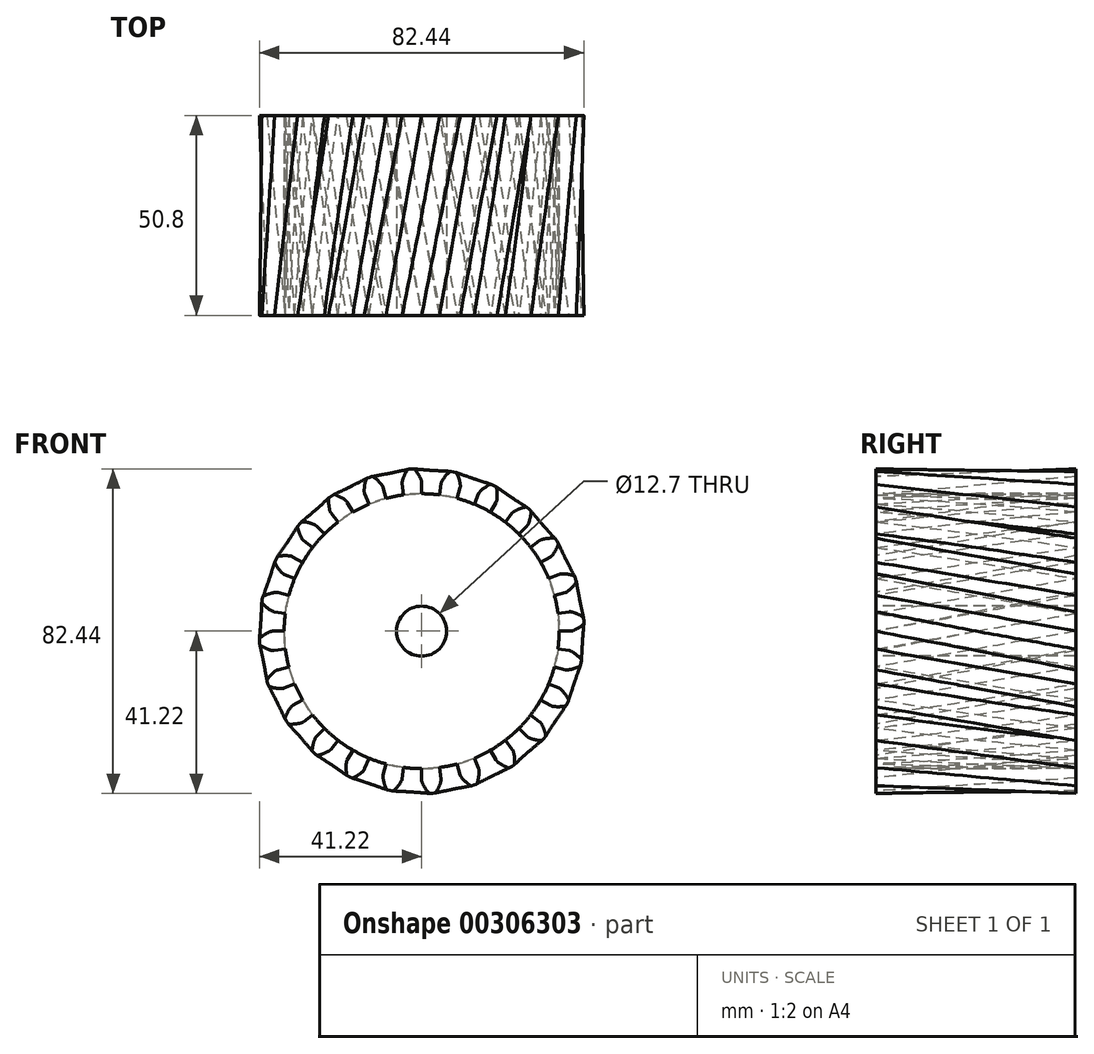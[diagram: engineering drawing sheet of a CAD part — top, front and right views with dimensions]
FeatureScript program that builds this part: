
annotation { "Feature Type Name" : "Feature", "Feature Type Description" : "" }
export const myFeature = defineFeature(function(context is Context, id is Id, definition is map)
    precondition{}
    {
        {
            var Q0;
            Q0=qCreatedBy(makeId("Front.planeOp"),FACE);
            var sketch = newSketch(context, id + "F0", { "sketchPlane" : qUnion([Q0])});
            skCircle(sketch, "E0", {"center": v(0, 0) * mm, "radius": 34.93 * mm});
            skArc(sketch, "E1.trimOffspring", {"start": v(-0.11, 38.4) * mm, "mid": v(-0.8, 39.79) * mm, "end": v(-1.72, 41.04) * mm});
            skLineSegment(sketch, "E2", {"start": v(0, 37.8) * mm, "end": v(0, 34.93) * mm});
            skLineSegment(sketch, "E3", {"start": v(-2.13, 41.22) * mm, "end": v(-2.7, 41.2) * mm});
            skArc(sketch, "E4.MirrorCS", {"start": v(-4.9, 38.09) * mm, "mid": v(-4.4, 39.55) * mm, "end": v(-3.65, 40.92) * mm});
            skLineSegment(sketch, "E5.MirrorCS", {"start": v(-4.93, 37.48) * mm, "end": v(-4.56, 34.63) * mm});
            skLineSegment(sketch, "E6.MirrorCS", {"start": v(-3.27, 41.15) * mm, "end": v(-2.7, 41.2) * mm});
            skPoint(sketch, "E7.visualSharp", {"position": v(-3.51, 41.13) * mm});
            skArc(sketch, "E7.filletArc", {"start": v(-3.27, 41.15) * mm, "mid": v(-3.49, 41.08) * mm, "end": v(-3.65, 40.92) * mm});
            skPoint(sketch, "E8.visualSharp", {"position": v(-1.89, 41.23) * mm});
            skArc(sketch, "E8.filletArc", {"start": v(-1.72, 41.04) * mm, "mid": v(-1.9, 41.18) * mm, "end": v(-2.13, 41.22) * mm});
            skPoint(sketch, "E9.visualSharp", {"position": v(-4.97, 37.77) * mm});
            skArc(sketch, "E9.filletArc", {"start": v(-4.9, 38.09) * mm, "mid": v(-4.95, 37.79) * mm, "end": v(-4.93, 37.48) * mm});
            skPoint(sketch, "E10.visualSharp", {"position": v(0, 38.1) * mm});
            skArc(sketch, "E10.filletArc", {"start": v(0, 37.8) * mm, "mid": v(-0.03, 38.1) * mm, "end": v(-0.11, 38.4) * mm});
            skSolve(sketch);
        }
        {
            var Q0;
            {var subQ0=sQuery(id+"F0.wireOp",EDGE,"E0");var subQ1=makeQuery(id+"F0.imprint","INTERSECT",VERTEX,{"derivedFrom":[subQ0,sQuery(id+"F0.wireOp",EDGE,"E2")]});Q0=makeQuery(id+"F0.imprint","IMPRINT",FACE,{"disambiguationData":[TD([[makeQuery(id+"F0.imprint","IMPRINT",EDGE,{"disambiguationData":[TD([[subQ1,-1.0]])],"derivedFrom":subQ0}),1.0]])]});}
            cPlane(context, id + "F1", {"entities" : qUnion([Q0]), "cplaneType" : CPlaneType.OFFSET, "offset" : 50.8 * mm, "width" : 152.4 * mm, "height" : 152.4 * mm});
        }
        {
            var Q0;
            Q0=qCreatedBy(id+"F1.planeOp",FACE);
            var sketch = newSketch(context, id + "F2", { "sketchPlane" : qUnion([Q0])});
            skCircle(sketch, "E11.0", {"center": v(0, 0) * mm, "radius": 34.93 * mm});
            skArc(sketch, "E12.0.0", {"start": v(-3.65, 40.92) * mm, "mid": v(-4.4, 39.55) * mm, "end": v(-4.9, 38.09) * mm});
            skArc(sketch, "E12.0.1", {"start": v(-4.9, 38.09) * mm, "mid": v(-4.95, 37.79) * mm, "end": v(-4.93, 37.48) * mm});
            skLineSegment(sketch, "E12.0.2", {"start": v(-4.93, 37.48) * mm, "end": v(-4.56, 34.63) * mm});
            skArc(sketch, "E12.0.3", {"start": v(-4.56, 34.63) * mm, "mid": v(-2.28, 34.85) * mm, "end": v(0, 34.93) * mm});
            skLineSegment(sketch, "E12.0.4", {"start": v(0, 34.93) * mm, "end": v(0, 37.8) * mm});
            skArc(sketch, "E12.0.5", {"start": v(0, 37.8) * mm, "mid": v(-0.03, 38.1) * mm, "end": v(-0.11, 38.4) * mm});
            skArc(sketch, "E12.0.6", {"start": v(-0.11, 38.4) * mm, "mid": v(-0.8, 39.79) * mm, "end": v(-1.72, 41.04) * mm});
            skArc(sketch, "E12.0.7", {"start": v(-1.72, 41.04) * mm, "mid": v(-1.9, 41.18) * mm, "end": v(-2.13, 41.22) * mm});
            skLineSegment(sketch, "E12.0.8", {"start": v(-2.13, 41.22) * mm, "end": v(-2.7, 41.2) * mm});
            skLineSegment(sketch, "E12.0.9", {"start": v(-2.7, 41.2) * mm, "end": v(-3.27, 41.15) * mm});
            skArc(sketch, "E12.0.10", {"start": v(-3.27, 41.15) * mm, "mid": v(-3.49, 41.08) * mm, "end": v(-3.65, 40.92) * mm});
            skLineSegment(sketch, "E13.1.0", {"start": v(-9.04, 33.73) * mm, "end": v(-9.79, 36.52) * mm});
            skArc(sketch, "E13.1.1", {"start": v(-10.05, 37.06) * mm, "mid": v(-11.08, 38.22) * mm, "end": v(-12.29, 39.2) * mm});
            skArc(sketch, "E13.1.2", {"start": v(-14.12, 38.58) * mm, "mid": v(-14.48, 37.07) * mm, "end": v(-14.59, 35.52) * mm});
            skLineSegment(sketch, "E13.1.3", {"start": v(-14.47, 34.93) * mm, "end": v(-13.37, 32.27) * mm});
            skArc(sketch, "E13.1.4", {"start": v(-14.59, 35.52) * mm, "mid": v(-14.56, 35.22) * mm, "end": v(-14.47, 34.93) * mm});
            skArc(sketch, "E13.1.5", {"start": v(-9.79, 36.52) * mm, "mid": v(-9.9, 36.8) * mm, "end": v(-10.05, 37.06) * mm});
            skArc(sketch, "E13.1.6", {"start": v(-12.29, 39.2) * mm, "mid": v(-12.5, 39.28) * mm, "end": v(-12.73, 39.26) * mm});
            skLineSegment(sketch, "E13.1.7", {"start": v(-12.73, 39.26) * mm, "end": v(-13.27, 39.1) * mm});
            skLineSegment(sketch, "E13.1.8", {"start": v(-13.27, 39.1) * mm, "end": v(-13.8, 38.9) * mm});
            skArc(sketch, "E13.1.9", {"start": v(-13.8, 38.9) * mm, "mid": v(-14, 38.77) * mm, "end": v(-14.12, 38.58) * mm});
            skLineSegment(sketch, "E13.2.0", {"start": v(-17.46, 30.25) * mm, "end": v(-18.9, 32.74) * mm});
            skArc(sketch, "E13.2.1", {"start": v(-19.3, 33.2) * mm, "mid": v(-20.6, 34.05) * mm, "end": v(-22.01, 34.68) * mm});
            skArc(sketch, "E13.2.2", {"start": v(-23.62, 33.61) * mm, "mid": v(-23.58, 32.06) * mm, "end": v(-23.29, 30.53) * mm});
            skLineSegment(sketch, "E13.2.3", {"start": v(-23.02, 30) * mm, "end": v(-21.26, 27.7) * mm});
            skArc(sketch, "E13.2.4", {"start": v(-23.29, 30.53) * mm, "mid": v(-23.18, 30.25) * mm, "end": v(-23.02, 30) * mm});
            skArc(sketch, "E13.2.5", {"start": v(-18.9, 32.74) * mm, "mid": v(-19.08, 32.99) * mm, "end": v(-19.3, 33.2) * mm});
            skArc(sketch, "E13.2.6", {"start": v(-22.01, 34.68) * mm, "mid": v(-22.24, 34.7) * mm, "end": v(-22.45, 34.63) * mm});
            skLineSegment(sketch, "E13.2.7", {"start": v(-22.45, 34.63) * mm, "end": v(-22.94, 34.33) * mm});
            skLineSegment(sketch, "E13.2.8", {"start": v(-22.94, 34.33) * mm, "end": v(-23.4, 34) * mm});
            skArc(sketch, "E13.2.9", {"start": v(-23.4, 34) * mm, "mid": v(-23.56, 33.83) * mm, "end": v(-23.62, 33.61) * mm});
            skLineSegment(sketch, "E13.3.0", {"start": v(-24.7, 24.7) * mm, "end": v(-26.73, 26.73) * mm});
            skArc(sketch, "E13.3.1", {"start": v(-27.23, 27.07) * mm, "mid": v(-28.7, 27.56) * mm, "end": v(-30.24, 27.8) * mm});
            skArc(sketch, "E13.3.2", {"start": v(-31.51, 26.35) * mm, "mid": v(-31.07, 24.86) * mm, "end": v(-30.4, 23.47) * mm});
            skLineSegment(sketch, "E13.3.3", {"start": v(-30, 23.02) * mm, "end": v(-27.7, 21.26) * mm});
            skArc(sketch, "E13.3.4", {"start": v(-30.4, 23.47) * mm, "mid": v(-30.22, 23.22) * mm, "end": v(-30, 23.02) * mm});
            skArc(sketch, "E13.3.5", {"start": v(-26.73, 26.73) * mm, "mid": v(-26.97, 26.93) * mm, "end": v(-27.23, 27.07) * mm});
            skArc(sketch, "E13.3.6", {"start": v(-30.24, 27.8) * mm, "mid": v(-30.47, 27.77) * mm, "end": v(-30.65, 27.64) * mm});
            skLineSegment(sketch, "E13.3.7", {"start": v(-30.65, 27.64) * mm, "end": v(-31.04, 27.22) * mm});
            skLineSegment(sketch, "E13.3.8", {"start": v(-31.04, 27.22) * mm, "end": v(-31.4, 26.78) * mm});
            skArc(sketch, "E13.3.9", {"start": v(-31.4, 26.78) * mm, "mid": v(-31.51, 26.58) * mm, "end": v(-31.51, 26.35) * mm});
            skLineSegment(sketch, "E13.4.0", {"start": v(-30.25, 17.46) * mm, "end": v(-32.74, 18.9) * mm});
            skArc(sketch, "E13.4.1", {"start": v(-33.31, 19.1) * mm, "mid": v(-34.86, 19.2) * mm, "end": v(-36.4, 19.03) * mm});
            skArc(sketch, "E13.4.2", {"start": v(-37.26, 17.3) * mm, "mid": v(-36.45, 15.97) * mm, "end": v(-35.43, 14.8) * mm});
            skLineSegment(sketch, "E13.4.3", {"start": v(-34.93, 14.47) * mm, "end": v(-32.27, 13.37) * mm});
            skArc(sketch, "E13.4.4", {"start": v(-35.43, 14.8) * mm, "mid": v(-35.2, 14.61) * mm, "end": v(-34.93, 14.47) * mm});
            skArc(sketch, "E13.4.5", {"start": v(-32.74, 18.9) * mm, "mid": v(-33.02, 19.03) * mm, "end": v(-33.31, 19.1) * mm});
            skArc(sketch, "E13.4.6", {"start": v(-36.4, 19.03) * mm, "mid": v(-36.62, 18.94) * mm, "end": v(-36.76, 18.77) * mm});
            skLineSegment(sketch, "E13.4.7", {"start": v(-36.76, 18.77) * mm, "end": v(-37.03, 18.26) * mm});
            skLineSegment(sketch, "E13.4.8", {"start": v(-37.03, 18.26) * mm, "end": v(-37.27, 17.74) * mm});
            skArc(sketch, "E13.4.9", {"start": v(-37.27, 17.74) * mm, "mid": v(-37.32, 17.52) * mm, "end": v(-37.26, 17.3) * mm});
            skLineSegment(sketch, "E13.5.0", {"start": v(-33.73, 9.04) * mm, "end": v(-36.52, 9.79) * mm});
            skArc(sketch, "E13.5.1", {"start": v(-37.12, 9.83) * mm, "mid": v(-38.64, 9.52) * mm, "end": v(-40.1, 8.96) * mm});
            skArc(sketch, "E13.5.2", {"start": v(-40.47, 7.06) * mm, "mid": v(-39.34, 6) * mm, "end": v(-38.06, 5.13) * mm});
            skLineSegment(sketch, "E13.5.3", {"start": v(-37.48, 4.93) * mm, "end": v(-34.63, 4.56) * mm});
            skArc(sketch, "E13.5.4", {"start": v(-38.06, 5.13) * mm, "mid": v(-37.78, 5) * mm, "end": v(-37.48, 4.93) * mm});
            skArc(sketch, "E13.5.5", {"start": v(-36.52, 9.79) * mm, "mid": v(-36.82, 9.84) * mm, "end": v(-37.12, 9.83) * mm});
            skArc(sketch, "E13.5.6", {"start": v(-40.1, 8.96) * mm, "mid": v(-40.27, 8.82) * mm, "end": v(-40.37, 8.61) * mm});
            skLineSegment(sketch, "E13.5.7", {"start": v(-40.37, 8.61) * mm, "end": v(-40.49, 8.05) * mm});
            skLineSegment(sketch, "E13.5.8", {"start": v(-40.49, 8.05) * mm, "end": v(-40.6, 7.5) * mm});
            skArc(sketch, "E13.5.9", {"start": v(-40.6, 7.5) * mm, "mid": v(-40.58, 7.26) * mm, "end": v(-40.47, 7.06) * mm});
            skLineSegment(sketch, "E13.6.0", {"start": v(-34.93, 0) * mm, "end": v(-37.8, 0) * mm});
            skArc(sketch, "E13.6.1", {"start": v(-38.4, -0.11) * mm, "mid": v(-39.79, -0.8) * mm, "end": v(-41.04, -1.72) * mm});
            skArc(sketch, "E13.6.2", {"start": v(-40.92, -3.65) * mm, "mid": v(-39.55, -4.4) * mm, "end": v(-38.09, -4.9) * mm});
            skLineSegment(sketch, "E13.6.3", {"start": v(-37.48, -4.93) * mm, "end": v(-34.63, -4.56) * mm});
            skArc(sketch, "E13.6.4", {"start": v(-38.09, -4.9) * mm, "mid": v(-37.79, -4.95) * mm, "end": v(-37.48, -4.93) * mm});
            skArc(sketch, "E13.6.5", {"start": v(-37.8, 0) * mm, "mid": v(-38.1, -0.03) * mm, "end": v(-38.4, -0.11) * mm});
            skArc(sketch, "E13.6.6", {"start": v(-41.04, -1.72) * mm, "mid": v(-41.18, -1.9) * mm, "end": v(-41.22, -2.13) * mm});
            skLineSegment(sketch, "E13.6.7", {"start": v(-41.22, -2.13) * mm, "end": v(-41.2, -2.7) * mm});
            skLineSegment(sketch, "E13.6.8", {"start": v(-41.2, -2.7) * mm, "end": v(-41.15, -3.27) * mm});
            skArc(sketch, "E13.6.9", {"start": v(-41.15, -3.27) * mm, "mid": v(-41.08, -3.49) * mm, "end": v(-40.92, -3.65) * mm});
            skLineSegment(sketch, "E13.7.0", {"start": v(-33.73, -9.04) * mm, "end": v(-36.52, -9.79) * mm});
            skArc(sketch, "E13.7.1", {"start": v(-37.06, -10.05) * mm, "mid": v(-38.22, -11.08) * mm, "end": v(-39.2, -12.29) * mm});
            skArc(sketch, "E13.7.2", {"start": v(-38.58, -14.12) * mm, "mid": v(-37.07, -14.48) * mm, "end": v(-35.52, -14.59) * mm});
            skLineSegment(sketch, "E13.7.3", {"start": v(-34.93, -14.47) * mm, "end": v(-32.27, -13.37) * mm});
            skArc(sketch, "E13.7.4", {"start": v(-35.52, -14.59) * mm, "mid": v(-35.22, -14.56) * mm, "end": v(-34.93, -14.47) * mm});
            skArc(sketch, "E13.7.5", {"start": v(-36.52, -9.79) * mm, "mid": v(-36.8, -9.9) * mm, "end": v(-37.06, -10.05) * mm});
            skArc(sketch, "E13.7.6", {"start": v(-39.2, -12.29) * mm, "mid": v(-39.28, -12.5) * mm, "end": v(-39.26, -12.73) * mm});
            skLineSegment(sketch, "E13.7.7", {"start": v(-39.26, -12.73) * mm, "end": v(-39.1, -13.27) * mm});
            skLineSegment(sketch, "E13.7.8", {"start": v(-39.1, -13.27) * mm, "end": v(-38.9, -13.8) * mm});
            skArc(sketch, "E13.7.9", {"start": v(-38.9, -13.8) * mm, "mid": v(-38.77, -14) * mm, "end": v(-38.58, -14.12) * mm});
            skLineSegment(sketch, "E13.8.0", {"start": v(-30.25, -17.46) * mm, "end": v(-32.74, -18.9) * mm});
            skArc(sketch, "E13.8.1", {"start": v(-33.2, -19.3) * mm, "mid": v(-34.05, -20.6) * mm, "end": v(-34.68, -22.01) * mm});
            skArc(sketch, "E13.8.2", {"start": v(-33.61, -23.62) * mm, "mid": v(-32.06, -23.58) * mm, "end": v(-30.53, -23.29) * mm});
            skLineSegment(sketch, "E13.8.3", {"start": v(-30, -23.02) * mm, "end": v(-27.7, -21.26) * mm});
            skArc(sketch, "E13.8.4", {"start": v(-30.53, -23.29) * mm, "mid": v(-30.25, -23.18) * mm, "end": v(-30, -23.02) * mm});
            skArc(sketch, "E13.8.5", {"start": v(-32.74, -18.9) * mm, "mid": v(-32.99, -19.08) * mm, "end": v(-33.2, -19.3) * mm});
            skArc(sketch, "E13.8.6", {"start": v(-34.68, -22.01) * mm, "mid": v(-34.7, -22.24) * mm, "end": v(-34.63, -22.45) * mm});
            skLineSegment(sketch, "E13.8.7", {"start": v(-34.63, -22.45) * mm, "end": v(-34.33, -22.94) * mm});
            skLineSegment(sketch, "E13.8.8", {"start": v(-34.33, -22.94) * mm, "end": v(-34, -23.4) * mm});
            skArc(sketch, "E13.8.9", {"start": v(-34, -23.4) * mm, "mid": v(-33.83, -23.56) * mm, "end": v(-33.61, -23.62) * mm});
            skLineSegment(sketch, "E13.9.0", {"start": v(-24.7, -24.7) * mm, "end": v(-26.73, -26.73) * mm});
            skArc(sketch, "E13.9.1", {"start": v(-27.07, -27.23) * mm, "mid": v(-27.56, -28.7) * mm, "end": v(-27.8, -30.24) * mm});
            skArc(sketch, "E13.9.2", {"start": v(-26.35, -31.51) * mm, "mid": v(-24.86, -31.07) * mm, "end": v(-23.47, -30.4) * mm});
            skLineSegment(sketch, "E13.9.3", {"start": v(-23.02, -30) * mm, "end": v(-21.26, -27.7) * mm});
            skArc(sketch, "E13.9.4", {"start": v(-23.47, -30.4) * mm, "mid": v(-23.22, -30.22) * mm, "end": v(-23.02, -30) * mm});
            skArc(sketch, "E13.9.5", {"start": v(-26.73, -26.73) * mm, "mid": v(-26.93, -26.97) * mm, "end": v(-27.07, -27.23) * mm});
            skArc(sketch, "E13.9.6", {"start": v(-27.8, -30.24) * mm, "mid": v(-27.77, -30.47) * mm, "end": v(-27.64, -30.65) * mm});
            skLineSegment(sketch, "E13.9.7", {"start": v(-27.64, -30.65) * mm, "end": v(-27.22, -31.04) * mm});
            skLineSegment(sketch, "E13.9.8", {"start": v(-27.22, -31.04) * mm, "end": v(-26.78, -31.4) * mm});
            skArc(sketch, "E13.9.9", {"start": v(-26.78, -31.4) * mm, "mid": v(-26.58, -31.51) * mm, "end": v(-26.35, -31.51) * mm});
            skLineSegment(sketch, "E13.10.0", {"start": v(-17.46, -30.25) * mm, "end": v(-18.9, -32.74) * mm});
            skArc(sketch, "E13.10.1", {"start": v(-19.1, -33.31) * mm, "mid": v(-19.2, -34.86) * mm, "end": v(-19.03, -36.4) * mm});
            skArc(sketch, "E13.10.2", {"start": v(-17.3, -37.26) * mm, "mid": v(-15.97, -36.45) * mm, "end": v(-14.8, -35.43) * mm});
            skLineSegment(sketch, "E13.10.3", {"start": v(-14.47, -34.93) * mm, "end": v(-13.37, -32.27) * mm});
            skArc(sketch, "E13.10.4", {"start": v(-14.8, -35.43) * mm, "mid": v(-14.61, -35.2) * mm, "end": v(-14.47, -34.93) * mm});
            skArc(sketch, "E13.10.5", {"start": v(-18.9, -32.74) * mm, "mid": v(-19.03, -33.02) * mm, "end": v(-19.1, -33.31) * mm});
            skArc(sketch, "E13.10.6", {"start": v(-19.03, -36.4) * mm, "mid": v(-18.94, -36.62) * mm, "end": v(-18.77, -36.76) * mm});
            skLineSegment(sketch, "E13.10.7", {"start": v(-18.77, -36.76) * mm, "end": v(-18.26, -37.03) * mm});
            skLineSegment(sketch, "E13.10.8", {"start": v(-18.26, -37.03) * mm, "end": v(-17.74, -37.27) * mm});
            skArc(sketch, "E13.10.9", {"start": v(-17.74, -37.27) * mm, "mid": v(-17.52, -37.32) * mm, "end": v(-17.3, -37.26) * mm});
            skLineSegment(sketch, "E13.11.0", {"start": v(-9.04, -33.73) * mm, "end": v(-9.79, -36.52) * mm});
            skArc(sketch, "E13.11.1", {"start": v(-9.83, -37.12) * mm, "mid": v(-9.52, -38.64) * mm, "end": v(-8.96, -40.1) * mm});
            skArc(sketch, "E13.11.2", {"start": v(-7.06, -40.47) * mm, "mid": v(-6, -39.34) * mm, "end": v(-5.13, -38.06) * mm});
            skLineSegment(sketch, "E13.11.3", {"start": v(-4.93, -37.48) * mm, "end": v(-4.56, -34.63) * mm});
            skArc(sketch, "E13.11.4", {"start": v(-5.13, -38.06) * mm, "mid": v(-5, -37.78) * mm, "end": v(-4.93, -37.48) * mm});
            skArc(sketch, "E13.11.5", {"start": v(-9.79, -36.52) * mm, "mid": v(-9.84, -36.82) * mm, "end": v(-9.83, -37.12) * mm});
            skArc(sketch, "E13.11.6", {"start": v(-8.96, -40.1) * mm, "mid": v(-8.82, -40.27) * mm, "end": v(-8.61, -40.37) * mm});
            skLineSegment(sketch, "E13.11.7", {"start": v(-8.61, -40.37) * mm, "end": v(-8.05, -40.49) * mm});
            skLineSegment(sketch, "E13.11.8", {"start": v(-8.05, -40.49) * mm, "end": v(-7.5, -40.6) * mm});
            skArc(sketch, "E13.11.9", {"start": v(-7.5, -40.6) * mm, "mid": v(-7.26, -40.58) * mm, "end": v(-7.06, -40.47) * mm});
            skLineSegment(sketch, "E13.12.0", {"start": v(0, -34.93) * mm, "end": v(0, -37.8) * mm});
            skArc(sketch, "E13.12.1", {"start": v(0.11, -38.4) * mm, "mid": v(0.8, -39.79) * mm, "end": v(1.72, -41.04) * mm});
            skArc(sketch, "E13.12.2", {"start": v(3.65, -40.92) * mm, "mid": v(4.4, -39.55) * mm, "end": v(4.9, -38.09) * mm});
            skLineSegment(sketch, "E13.12.3", {"start": v(4.93, -37.48) * mm, "end": v(4.56, -34.63) * mm});
            skArc(sketch, "E13.12.4", {"start": v(4.9, -38.09) * mm, "mid": v(4.95, -37.79) * mm, "end": v(4.93, -37.48) * mm});
            skArc(sketch, "E13.12.5", {"start": v(0, -37.8) * mm, "mid": v(0.03, -38.1) * mm, "end": v(0.11, -38.4) * mm});
            skArc(sketch, "E13.12.6", {"start": v(1.72, -41.04) * mm, "mid": v(1.9, -41.18) * mm, "end": v(2.13, -41.22) * mm});
            skLineSegment(sketch, "E13.12.7", {"start": v(2.13, -41.22) * mm, "end": v(2.7, -41.2) * mm});
            skLineSegment(sketch, "E13.12.8", {"start": v(2.7, -41.2) * mm, "end": v(3.27, -41.15) * mm});
            skArc(sketch, "E13.12.9", {"start": v(3.27, -41.15) * mm, "mid": v(3.49, -41.08) * mm, "end": v(3.65, -40.92) * mm});
            skLineSegment(sketch, "E13.13.0", {"start": v(9.04, -33.73) * mm, "end": v(9.79, -36.52) * mm});
            skArc(sketch, "E13.13.1", {"start": v(10.05, -37.06) * mm, "mid": v(11.08, -38.22) * mm, "end": v(12.29, -39.2) * mm});
            skArc(sketch, "E13.13.2", {"start": v(14.12, -38.58) * mm, "mid": v(14.48, -37.07) * mm, "end": v(14.59, -35.52) * mm});
            skLineSegment(sketch, "E13.13.3", {"start": v(14.47, -34.93) * mm, "end": v(13.37, -32.27) * mm});
            skArc(sketch, "E13.13.4", {"start": v(14.59, -35.52) * mm, "mid": v(14.56, -35.22) * mm, "end": v(14.47, -34.93) * mm});
            skArc(sketch, "E13.13.5", {"start": v(9.79, -36.52) * mm, "mid": v(9.9, -36.8) * mm, "end": v(10.05, -37.06) * mm});
            skArc(sketch, "E13.13.6", {"start": v(12.29, -39.2) * mm, "mid": v(12.5, -39.28) * mm, "end": v(12.73, -39.26) * mm});
            skLineSegment(sketch, "E13.13.7", {"start": v(12.73, -39.26) * mm, "end": v(13.27, -39.1) * mm});
            skLineSegment(sketch, "E13.13.8", {"start": v(13.27, -39.1) * mm, "end": v(13.8, -38.9) * mm});
            skArc(sketch, "E13.13.9", {"start": v(13.8, -38.9) * mm, "mid": v(14, -38.77) * mm, "end": v(14.12, -38.58) * mm});
            skLineSegment(sketch, "E13.14.0", {"start": v(17.46, -30.25) * mm, "end": v(18.9, -32.74) * mm});
            skArc(sketch, "E13.14.1", {"start": v(19.3, -33.2) * mm, "mid": v(20.6, -34.05) * mm, "end": v(22.01, -34.68) * mm});
            skArc(sketch, "E13.14.2", {"start": v(23.62, -33.61) * mm, "mid": v(23.58, -32.06) * mm, "end": v(23.29, -30.53) * mm});
            skLineSegment(sketch, "E13.14.3", {"start": v(23.02, -30) * mm, "end": v(21.26, -27.7) * mm});
            skArc(sketch, "E13.14.4", {"start": v(23.29, -30.53) * mm, "mid": v(23.18, -30.25) * mm, "end": v(23.02, -30) * mm});
            skArc(sketch, "E13.14.5", {"start": v(18.9, -32.74) * mm, "mid": v(19.08, -32.99) * mm, "end": v(19.3, -33.2) * mm});
            skArc(sketch, "E13.14.6", {"start": v(22.01, -34.68) * mm, "mid": v(22.24, -34.7) * mm, "end": v(22.45, -34.63) * mm});
            skLineSegment(sketch, "E13.14.7", {"start": v(22.45, -34.63) * mm, "end": v(22.94, -34.33) * mm});
            skLineSegment(sketch, "E13.14.8", {"start": v(22.94, -34.33) * mm, "end": v(23.4, -34) * mm});
            skArc(sketch, "E13.14.9", {"start": v(23.4, -34) * mm, "mid": v(23.56, -33.83) * mm, "end": v(23.62, -33.61) * mm});
            skLineSegment(sketch, "E13.15.0", {"start": v(24.7, -24.7) * mm, "end": v(26.73, -26.73) * mm});
            skArc(sketch, "E13.15.1", {"start": v(27.23, -27.07) * mm, "mid": v(28.7, -27.56) * mm, "end": v(30.24, -27.8) * mm});
            skArc(sketch, "E13.15.2", {"start": v(31.51, -26.35) * mm, "mid": v(31.07, -24.86) * mm, "end": v(30.4, -23.47) * mm});
            skLineSegment(sketch, "E13.15.3", {"start": v(30, -23.02) * mm, "end": v(27.7, -21.26) * mm});
            skArc(sketch, "E13.15.4", {"start": v(30.4, -23.47) * mm, "mid": v(30.22, -23.22) * mm, "end": v(30, -23.02) * mm});
            skArc(sketch, "E13.15.5", {"start": v(26.73, -26.73) * mm, "mid": v(26.97, -26.93) * mm, "end": v(27.23, -27.07) * mm});
            skArc(sketch, "E13.15.6", {"start": v(30.24, -27.8) * mm, "mid": v(30.47, -27.77) * mm, "end": v(30.65, -27.64) * mm});
            skLineSegment(sketch, "E13.15.7", {"start": v(30.65, -27.64) * mm, "end": v(31.04, -27.22) * mm});
            skLineSegment(sketch, "E13.15.8", {"start": v(31.04, -27.22) * mm, "end": v(31.4, -26.78) * mm});
            skArc(sketch, "E13.15.9", {"start": v(31.4, -26.78) * mm, "mid": v(31.51, -26.58) * mm, "end": v(31.51, -26.35) * mm});
            skLineSegment(sketch, "E13.16.0", {"start": v(30.25, -17.46) * mm, "end": v(32.74, -18.9) * mm});
            skArc(sketch, "E13.16.1", {"start": v(33.31, -19.1) * mm, "mid": v(34.86, -19.2) * mm, "end": v(36.4, -19.03) * mm});
            skArc(sketch, "E13.16.2", {"start": v(37.26, -17.3) * mm, "mid": v(36.45, -15.97) * mm, "end": v(35.43, -14.8) * mm});
            skLineSegment(sketch, "E13.16.3", {"start": v(34.93, -14.47) * mm, "end": v(32.27, -13.37) * mm});
            skArc(sketch, "E13.16.4", {"start": v(35.43, -14.8) * mm, "mid": v(35.2, -14.61) * mm, "end": v(34.93, -14.47) * mm});
            skArc(sketch, "E13.16.5", {"start": v(32.74, -18.9) * mm, "mid": v(33.02, -19.03) * mm, "end": v(33.31, -19.1) * mm});
            skArc(sketch, "E13.16.6", {"start": v(36.4, -19.03) * mm, "mid": v(36.62, -18.94) * mm, "end": v(36.76, -18.77) * mm});
            skLineSegment(sketch, "E13.16.7", {"start": v(36.76, -18.77) * mm, "end": v(37.03, -18.26) * mm});
            skLineSegment(sketch, "E13.16.8", {"start": v(37.03, -18.26) * mm, "end": v(37.27, -17.74) * mm});
            skArc(sketch, "E13.16.9", {"start": v(37.27, -17.74) * mm, "mid": v(37.32, -17.52) * mm, "end": v(37.26, -17.3) * mm});
            skLineSegment(sketch, "E13.17.0", {"start": v(33.73, -9.04) * mm, "end": v(36.52, -9.79) * mm});
            skArc(sketch, "E13.17.1", {"start": v(37.12, -9.83) * mm, "mid": v(38.64, -9.52) * mm, "end": v(40.1, -8.96) * mm});
            skArc(sketch, "E13.17.2", {"start": v(40.47, -7.06) * mm, "mid": v(39.34, -6) * mm, "end": v(38.06, -5.13) * mm});
            skLineSegment(sketch, "E13.17.3", {"start": v(37.48, -4.93) * mm, "end": v(34.63, -4.56) * mm});
            skArc(sketch, "E13.17.4", {"start": v(38.06, -5.13) * mm, "mid": v(37.78, -5) * mm, "end": v(37.48, -4.93) * mm});
            skArc(sketch, "E13.17.5", {"start": v(36.52, -9.79) * mm, "mid": v(36.82, -9.84) * mm, "end": v(37.12, -9.83) * mm});
            skArc(sketch, "E13.17.6", {"start": v(40.1, -8.96) * mm, "mid": v(40.27, -8.82) * mm, "end": v(40.37, -8.61) * mm});
            skLineSegment(sketch, "E13.17.7", {"start": v(40.37, -8.61) * mm, "end": v(40.49, -8.05) * mm});
            skLineSegment(sketch, "E13.17.8", {"start": v(40.49, -8.05) * mm, "end": v(40.6, -7.5) * mm});
            skArc(sketch, "E13.17.9", {"start": v(40.6, -7.5) * mm, "mid": v(40.58, -7.26) * mm, "end": v(40.47, -7.06) * mm});
            skLineSegment(sketch, "E13.18.0", {"start": v(34.93, 0) * mm, "end": v(37.8, 0) * mm});
            skArc(sketch, "E13.18.1", {"start": v(38.4, 0.11) * mm, "mid": v(39.79, 0.8) * mm, "end": v(41.04, 1.72) * mm});
            skArc(sketch, "E13.18.2", {"start": v(40.92, 3.65) * mm, "mid": v(39.55, 4.4) * mm, "end": v(38.09, 4.9) * mm});
            skLineSegment(sketch, "E13.18.3", {"start": v(37.48, 4.93) * mm, "end": v(34.63, 4.56) * mm});
            skArc(sketch, "E13.18.4", {"start": v(38.09, 4.9) * mm, "mid": v(37.79, 4.95) * mm, "end": v(37.48, 4.93) * mm});
            skArc(sketch, "E13.18.5", {"start": v(37.8, 0) * mm, "mid": v(38.1, 0.03) * mm, "end": v(38.4, 0.11) * mm});
            skArc(sketch, "E13.18.6", {"start": v(41.04, 1.72) * mm, "mid": v(41.18, 1.9) * mm, "end": v(41.22, 2.13) * mm});
            skLineSegment(sketch, "E13.18.7", {"start": v(41.22, 2.13) * mm, "end": v(41.2, 2.7) * mm});
            skLineSegment(sketch, "E13.18.8", {"start": v(41.2, 2.7) * mm, "end": v(41.15, 3.27) * mm});
            skArc(sketch, "E13.18.9", {"start": v(41.15, 3.27) * mm, "mid": v(41.08, 3.49) * mm, "end": v(40.92, 3.65) * mm});
            skLineSegment(sketch, "E13.19.0", {"start": v(33.73, 9.04) * mm, "end": v(36.52, 9.79) * mm});
            skArc(sketch, "E13.19.1", {"start": v(37.06, 10.05) * mm, "mid": v(38.22, 11.08) * mm, "end": v(39.2, 12.29) * mm});
            skArc(sketch, "E13.19.2", {"start": v(38.58, 14.12) * mm, "mid": v(37.07, 14.48) * mm, "end": v(35.52, 14.59) * mm});
            skLineSegment(sketch, "E13.19.3", {"start": v(34.93, 14.47) * mm, "end": v(32.27, 13.37) * mm});
            skArc(sketch, "E13.19.4", {"start": v(35.52, 14.59) * mm, "mid": v(35.22, 14.56) * mm, "end": v(34.93, 14.47) * mm});
            skArc(sketch, "E13.19.5", {"start": v(36.52, 9.79) * mm, "mid": v(36.8, 9.9) * mm, "end": v(37.06, 10.05) * mm});
            skArc(sketch, "E13.19.6", {"start": v(39.2, 12.29) * mm, "mid": v(39.28, 12.5) * mm, "end": v(39.26, 12.73) * mm});
            skLineSegment(sketch, "E13.19.7", {"start": v(39.26, 12.73) * mm, "end": v(39.1, 13.27) * mm});
            skLineSegment(sketch, "E13.19.8", {"start": v(39.1, 13.27) * mm, "end": v(38.9, 13.8) * mm});
            skArc(sketch, "E13.19.9", {"start": v(38.9, 13.8) * mm, "mid": v(38.77, 14) * mm, "end": v(38.58, 14.12) * mm});
            skLineSegment(sketch, "E13.20.0", {"start": v(30.25, 17.46) * mm, "end": v(32.74, 18.9) * mm});
            skArc(sketch, "E13.20.1", {"start": v(33.2, 19.3) * mm, "mid": v(34.05, 20.6) * mm, "end": v(34.68, 22.01) * mm});
            skArc(sketch, "E13.20.2", {"start": v(33.61, 23.62) * mm, "mid": v(32.06, 23.58) * mm, "end": v(30.53, 23.29) * mm});
            skLineSegment(sketch, "E13.20.3", {"start": v(30, 23.02) * mm, "end": v(27.7, 21.26) * mm});
            skArc(sketch, "E13.20.4", {"start": v(30.53, 23.29) * mm, "mid": v(30.25, 23.18) * mm, "end": v(30, 23.02) * mm});
            skArc(sketch, "E13.20.5", {"start": v(32.74, 18.9) * mm, "mid": v(32.99, 19.08) * mm, "end": v(33.2, 19.3) * mm});
            skArc(sketch, "E13.20.6", {"start": v(34.68, 22.01) * mm, "mid": v(34.7, 22.24) * mm, "end": v(34.63, 22.45) * mm});
            skLineSegment(sketch, "E13.20.7", {"start": v(34.63, 22.45) * mm, "end": v(34.33, 22.94) * mm});
            skLineSegment(sketch, "E13.20.8", {"start": v(34.33, 22.94) * mm, "end": v(34, 23.4) * mm});
            skArc(sketch, "E13.20.9", {"start": v(34, 23.4) * mm, "mid": v(33.83, 23.56) * mm, "end": v(33.61, 23.62) * mm});
            skLineSegment(sketch, "E13.21.0", {"start": v(24.7, 24.7) * mm, "end": v(26.73, 26.73) * mm});
            skArc(sketch, "E13.21.1", {"start": v(27.07, 27.23) * mm, "mid": v(27.56, 28.7) * mm, "end": v(27.8, 30.24) * mm});
            skArc(sketch, "E13.21.2", {"start": v(26.35, 31.51) * mm, "mid": v(24.86, 31.07) * mm, "end": v(23.47, 30.4) * mm});
            skLineSegment(sketch, "E13.21.3", {"start": v(23.02, 30) * mm, "end": v(21.26, 27.7) * mm});
            skArc(sketch, "E13.21.4", {"start": v(23.47, 30.4) * mm, "mid": v(23.22, 30.22) * mm, "end": v(23.02, 30) * mm});
            skArc(sketch, "E13.21.5", {"start": v(26.73, 26.73) * mm, "mid": v(26.93, 26.97) * mm, "end": v(27.07, 27.23) * mm});
            skArc(sketch, "E13.21.6", {"start": v(27.8, 30.24) * mm, "mid": v(27.77, 30.47) * mm, "end": v(27.64, 30.65) * mm});
            skLineSegment(sketch, "E13.21.7", {"start": v(27.64, 30.65) * mm, "end": v(27.22, 31.04) * mm});
            skLineSegment(sketch, "E13.21.8", {"start": v(27.22, 31.04) * mm, "end": v(26.78, 31.4) * mm});
            skArc(sketch, "E13.21.9", {"start": v(26.78, 31.4) * mm, "mid": v(26.58, 31.51) * mm, "end": v(26.35, 31.51) * mm});
            skLineSegment(sketch, "E13.22.0", {"start": v(17.46, 30.25) * mm, "end": v(18.9, 32.74) * mm});
            skArc(sketch, "E13.22.1", {"start": v(19.1, 33.31) * mm, "mid": v(19.2, 34.86) * mm, "end": v(19.03, 36.4) * mm});
            skArc(sketch, "E13.22.2", {"start": v(17.3, 37.26) * mm, "mid": v(15.97, 36.45) * mm, "end": v(14.8, 35.43) * mm});
            skLineSegment(sketch, "E13.22.3", {"start": v(14.47, 34.93) * mm, "end": v(13.37, 32.27) * mm});
            skArc(sketch, "E13.22.4", {"start": v(14.8, 35.43) * mm, "mid": v(14.61, 35.2) * mm, "end": v(14.47, 34.93) * mm});
            skArc(sketch, "E13.22.5", {"start": v(18.9, 32.74) * mm, "mid": v(19.03, 33.02) * mm, "end": v(19.1, 33.31) * mm});
            skArc(sketch, "E13.22.6", {"start": v(19.03, 36.4) * mm, "mid": v(18.94, 36.62) * mm, "end": v(18.77, 36.76) * mm});
            skLineSegment(sketch, "E13.22.7", {"start": v(18.77, 36.76) * mm, "end": v(18.26, 37.03) * mm});
            skLineSegment(sketch, "E13.22.8", {"start": v(18.26, 37.03) * mm, "end": v(17.74, 37.27) * mm});
            skArc(sketch, "E13.22.9", {"start": v(17.74, 37.27) * mm, "mid": v(17.52, 37.32) * mm, "end": v(17.3, 37.26) * mm});
            skLineSegment(sketch, "E13.23.0", {"start": v(9.04, 33.73) * mm, "end": v(9.79, 36.52) * mm});
            skArc(sketch, "E13.23.1", {"start": v(9.83, 37.12) * mm, "mid": v(9.52, 38.64) * mm, "end": v(8.96, 40.1) * mm});
            skArc(sketch, "E13.23.2", {"start": v(7.06, 40.47) * mm, "mid": v(6, 39.34) * mm, "end": v(5.13, 38.06) * mm});
            skLineSegment(sketch, "E13.23.3", {"start": v(4.93, 37.48) * mm, "end": v(4.56, 34.63) * mm});
            skArc(sketch, "E13.23.4", {"start": v(5.13, 38.06) * mm, "mid": v(5, 37.78) * mm, "end": v(4.93, 37.48) * mm});
            skArc(sketch, "E13.23.5", {"start": v(9.79, 36.52) * mm, "mid": v(9.84, 36.82) * mm, "end": v(9.83, 37.12) * mm});
            skArc(sketch, "E13.23.6", {"start": v(8.96, 40.1) * mm, "mid": v(8.82, 40.27) * mm, "end": v(8.61, 40.37) * mm});
            skLineSegment(sketch, "E13.23.7", {"start": v(8.61, 40.37) * mm, "end": v(8.05, 40.49) * mm});
            skLineSegment(sketch, "E13.23.8", {"start": v(8.05, 40.49) * mm, "end": v(7.5, 40.6) * mm});
            skArc(sketch, "E13.23.9", {"start": v(7.5, 40.6) * mm, "mid": v(7.26, 40.58) * mm, "end": v(7.06, 40.47) * mm});
            skSolve(sketch);
        }
        {
            var Q0;
            {var subQ1=sQuery(id+"F2.wireOp",EDGE,"E13.1.0");Q0=makeQuery(id+"F2.imprint","IMPRINT",FACE,{"disambiguationData":[TD([[makeQuery(id+"F2.imprint","IMPRINT",EDGE,{"derivedFrom":subQ1}),1.0]])]});}
            var Q1;
            Q1=makeQuery(id+"F0.imprint","IMPRINT",FACE,{"disambiguationData":[TD([[makeQuery(id+"F0.imprint","IMPRINT",EDGE,{"derivedFrom":sQuery(id+"F0.wireOp",EDGE,"E1.trimOffspring")}),1.0]])]});
            loft(context, id + "F3", {"sheetProfilesArray" : [{ "sheetProfileEntities" : qUnion([Q0]) }, { "sheetProfileEntities" : qUnion([Q1]) }]});
        }
        {
            var Q0;
            Q0=qCreatedBy(id+"F1.planeOp",FACE);
            var sketch = newSketch(context, id + "F4", { "sketchPlane" : qUnion([Q0])});
            skCircle(sketch, "E14", {"center": v(0, 0) * mm, "radius": 34.93 * mm});
            skSolve(sketch);
        }
        {
            var Q0;
            Q0=makeQuery(id+"F4.imprint","IMPRINT",FACE,{"disambiguationData":[TD([[makeQuery(id+"F4.imprint","IMPRINT",EDGE,{"derivedFrom":sQuery(id+"F4.wireOp",EDGE,"E14")}),1.0]])]});
            var Q1;
            Q1=makeQuery(id+"F3.opLoft","CAP_FACE",FACE,{"disambiguationData":[OSD([makeQuery(id+"F0.imprint","IMPRINT",FACE,{"disambiguationData":[TD([[makeQuery(id+"F0.imprint","IMPRINT",EDGE,{"derivedFrom":sQuery(id+"F0.wireOp",EDGE,"E1.trimOffspring")}),1.0]])]})])],"isStart":true});
            extrude(context, id + "F5", {"entities" : qUnion([Q0]), "operationType" : NewBodyOperationType.ADD, "endBound" : BoundingType.UP_TO_SURFACE, "oppositeDirection" : true, "endBoundEntityFace" : qUnion([Q1]), "depth" : 25.4 * mm});
        }
        {
            var Q0;
            {var subQ1=sQuery(id+"F2.wireOp",EDGE,"E13.1.0");Q0=makeQuery(id+"F3.opLoft","SWEPT_BODY",BODY,{"disambiguationData":[OSD([makeQuery(id+"F0.imprint","IMPRINT",FACE,{"disambiguationData":[TD([[makeQuery(id+"F0.imprint","IMPRINT",EDGE,{"derivedFrom":sQuery(id+"F0.wireOp",EDGE,"E1.trimOffspring")}),1.0]])]}),makeQuery(id+"F2.imprint","IMPRINT",FACE,{"disambiguationData":[TD([[makeQuery(id+"F2.imprint","IMPRINT",EDGE,{"derivedFrom":subQ1}),1.0]])]})])]});}
            var Q1;
            Q1=makeQuery(id+"F5.opExtrude","SWEPT_FACE",FACE,{"disambiguationData":[OSD([sQuery(id+"F4.wireOp",EDGE,"E14")])]});
            circularPattern(context, id + "F6", {"entities" : qUnion([Q0]), "axis" : qUnion([Q1]), "angle" : 360 * degree, "instanceCount" : 24, "equalSpace" : true});
        }
        {
            var Q0;
            {var subQ1=sQuery(id+"F2.wireOp",EDGE,"E13.1.0");Q0=makeQuery(id+"F3.opLoft","SWEPT_BODY",BODY,{"disambiguationData":[OSD([makeQuery(id+"F0.imprint","IMPRINT",FACE,{"disambiguationData":[TD([[makeQuery(id+"F0.imprint","IMPRINT",EDGE,{"derivedFrom":sQuery(id+"F0.wireOp",EDGE,"E1.trimOffspring")}),1.0]])]}),makeQuery(id+"F2.imprint","IMPRINT",FACE,{"disambiguationData":[TD([[makeQuery(id+"F2.imprint","IMPRINT",EDGE,{"derivedFrom":subQ1}),1.0]])]})])]});}
            var Q1;
            {var subQ1=sQuery(id+"F2.wireOp",EDGE,"E13.1.0");Q1=makeQuery(id+"F6.opPattern","COPY",BODY,{"derivedFrom":makeQuery(id+"F3.opLoft","SWEPT_BODY",BODY,{"disambiguationData":[OSD([makeQuery(id+"F0.imprint","IMPRINT",FACE,{"disambiguationData":[TD([[makeQuery(id+"F0.imprint","IMPRINT",EDGE,{"derivedFrom":sQuery(id+"F0.wireOp",EDGE,"E1.trimOffspring")}),1.0]])]}),makeQuery(id+"F2.imprint","IMPRINT",FACE,{"disambiguationData":[TD([[makeQuery(id+"F2.imprint","IMPRINT",EDGE,{"derivedFrom":subQ1}),1.0]])]})])]}),"instanceName":"1"});}
            var Q2;
            {var subQ1=sQuery(id+"F2.wireOp",EDGE,"E13.1.0");Q2=makeQuery(id+"F6.opPattern","COPY",BODY,{"derivedFrom":makeQuery(id+"F3.opLoft","SWEPT_BODY",BODY,{"disambiguationData":[OSD([makeQuery(id+"F0.imprint","IMPRINT",FACE,{"disambiguationData":[TD([[makeQuery(id+"F0.imprint","IMPRINT",EDGE,{"derivedFrom":sQuery(id+"F0.wireOp",EDGE,"E1.trimOffspring")}),1.0]])]}),makeQuery(id+"F2.imprint","IMPRINT",FACE,{"disambiguationData":[TD([[makeQuery(id+"F2.imprint","IMPRINT",EDGE,{"derivedFrom":subQ1}),1.0]])]})])]}),"instanceName":"23"});}
            var Q3;
            {var subQ1=sQuery(id+"F2.wireOp",EDGE,"E13.1.0");Q3=makeQuery(id+"F6.opPattern","COPY",BODY,{"derivedFrom":makeQuery(id+"F3.opLoft","SWEPT_BODY",BODY,{"disambiguationData":[OSD([makeQuery(id+"F0.imprint","IMPRINT",FACE,{"disambiguationData":[TD([[makeQuery(id+"F0.imprint","IMPRINT",EDGE,{"derivedFrom":sQuery(id+"F0.wireOp",EDGE,"E1.trimOffspring")}),1.0]])]}),makeQuery(id+"F2.imprint","IMPRINT",FACE,{"disambiguationData":[TD([[makeQuery(id+"F2.imprint","IMPRINT",EDGE,{"derivedFrom":subQ1}),1.0]])]})])]}),"instanceName":"22"});}
            var Q4;
            {var subQ1=sQuery(id+"F2.wireOp",EDGE,"E13.1.0");Q4=makeQuery(id+"F6.opPattern","COPY",BODY,{"derivedFrom":makeQuery(id+"F3.opLoft","SWEPT_BODY",BODY,{"disambiguationData":[OSD([makeQuery(id+"F0.imprint","IMPRINT",FACE,{"disambiguationData":[TD([[makeQuery(id+"F0.imprint","IMPRINT",EDGE,{"derivedFrom":sQuery(id+"F0.wireOp",EDGE,"E1.trimOffspring")}),1.0]])]}),makeQuery(id+"F2.imprint","IMPRINT",FACE,{"disambiguationData":[TD([[makeQuery(id+"F2.imprint","IMPRINT",EDGE,{"derivedFrom":subQ1}),1.0]])]})])]}),"instanceName":"21"});}
            var Q5;
            {var subQ1=sQuery(id+"F2.wireOp",EDGE,"E13.1.0");Q5=makeQuery(id+"F6.opPattern","COPY",BODY,{"derivedFrom":makeQuery(id+"F3.opLoft","SWEPT_BODY",BODY,{"disambiguationData":[OSD([makeQuery(id+"F0.imprint","IMPRINT",FACE,{"disambiguationData":[TD([[makeQuery(id+"F0.imprint","IMPRINT",EDGE,{"derivedFrom":sQuery(id+"F0.wireOp",EDGE,"E1.trimOffspring")}),1.0]])]}),makeQuery(id+"F2.imprint","IMPRINT",FACE,{"disambiguationData":[TD([[makeQuery(id+"F2.imprint","IMPRINT",EDGE,{"derivedFrom":subQ1}),1.0]])]})])]}),"instanceName":"20"});}
            var Q6;
            {var subQ1=sQuery(id+"F2.wireOp",EDGE,"E13.1.0");Q6=makeQuery(id+"F6.opPattern","COPY",BODY,{"derivedFrom":makeQuery(id+"F3.opLoft","SWEPT_BODY",BODY,{"disambiguationData":[OSD([makeQuery(id+"F0.imprint","IMPRINT",FACE,{"disambiguationData":[TD([[makeQuery(id+"F0.imprint","IMPRINT",EDGE,{"derivedFrom":sQuery(id+"F0.wireOp",EDGE,"E1.trimOffspring")}),1.0]])]}),makeQuery(id+"F2.imprint","IMPRINT",FACE,{"disambiguationData":[TD([[makeQuery(id+"F2.imprint","IMPRINT",EDGE,{"derivedFrom":subQ1}),1.0]])]})])]}),"instanceName":"19"});}
            var Q7;
            {var subQ1=sQuery(id+"F2.wireOp",EDGE,"E13.1.0");Q7=makeQuery(id+"F6.opPattern","COPY",BODY,{"derivedFrom":makeQuery(id+"F3.opLoft","SWEPT_BODY",BODY,{"disambiguationData":[OSD([makeQuery(id+"F0.imprint","IMPRINT",FACE,{"disambiguationData":[TD([[makeQuery(id+"F0.imprint","IMPRINT",EDGE,{"derivedFrom":sQuery(id+"F0.wireOp",EDGE,"E1.trimOffspring")}),1.0]])]}),makeQuery(id+"F2.imprint","IMPRINT",FACE,{"disambiguationData":[TD([[makeQuery(id+"F2.imprint","IMPRINT",EDGE,{"derivedFrom":subQ1}),1.0]])]})])]}),"instanceName":"18"});}
            var Q8;
            {var subQ1=sQuery(id+"F2.wireOp",EDGE,"E13.1.0");Q8=makeQuery(id+"F6.opPattern","COPY",BODY,{"derivedFrom":makeQuery(id+"F3.opLoft","SWEPT_BODY",BODY,{"disambiguationData":[OSD([makeQuery(id+"F0.imprint","IMPRINT",FACE,{"disambiguationData":[TD([[makeQuery(id+"F0.imprint","IMPRINT",EDGE,{"derivedFrom":sQuery(id+"F0.wireOp",EDGE,"E1.trimOffspring")}),1.0]])]}),makeQuery(id+"F2.imprint","IMPRINT",FACE,{"disambiguationData":[TD([[makeQuery(id+"F2.imprint","IMPRINT",EDGE,{"derivedFrom":subQ1}),1.0]])]})])]}),"instanceName":"17"});}
            var Q9;
            {var subQ1=sQuery(id+"F2.wireOp",EDGE,"E13.1.0");Q9=makeQuery(id+"F6.opPattern","COPY",BODY,{"derivedFrom":makeQuery(id+"F3.opLoft","SWEPT_BODY",BODY,{"disambiguationData":[OSD([makeQuery(id+"F0.imprint","IMPRINT",FACE,{"disambiguationData":[TD([[makeQuery(id+"F0.imprint","IMPRINT",EDGE,{"derivedFrom":sQuery(id+"F0.wireOp",EDGE,"E1.trimOffspring")}),1.0]])]}),makeQuery(id+"F2.imprint","IMPRINT",FACE,{"disambiguationData":[TD([[makeQuery(id+"F2.imprint","IMPRINT",EDGE,{"derivedFrom":subQ1}),1.0]])]})])]}),"instanceName":"16"});}
            var Q10;
            {var subQ1=sQuery(id+"F2.wireOp",EDGE,"E13.1.0");Q10=makeQuery(id+"F6.opPattern","COPY",BODY,{"derivedFrom":makeQuery(id+"F3.opLoft","SWEPT_BODY",BODY,{"disambiguationData":[OSD([makeQuery(id+"F0.imprint","IMPRINT",FACE,{"disambiguationData":[TD([[makeQuery(id+"F0.imprint","IMPRINT",EDGE,{"derivedFrom":sQuery(id+"F0.wireOp",EDGE,"E1.trimOffspring")}),1.0]])]}),makeQuery(id+"F2.imprint","IMPRINT",FACE,{"disambiguationData":[TD([[makeQuery(id+"F2.imprint","IMPRINT",EDGE,{"derivedFrom":subQ1}),1.0]])]})])]}),"instanceName":"15"});}
            var Q11;
            {var subQ1=sQuery(id+"F2.wireOp",EDGE,"E13.1.0");Q11=makeQuery(id+"F6.opPattern","COPY",BODY,{"derivedFrom":makeQuery(id+"F3.opLoft","SWEPT_BODY",BODY,{"disambiguationData":[OSD([makeQuery(id+"F0.imprint","IMPRINT",FACE,{"disambiguationData":[TD([[makeQuery(id+"F0.imprint","IMPRINT",EDGE,{"derivedFrom":sQuery(id+"F0.wireOp",EDGE,"E1.trimOffspring")}),1.0]])]}),makeQuery(id+"F2.imprint","IMPRINT",FACE,{"disambiguationData":[TD([[makeQuery(id+"F2.imprint","IMPRINT",EDGE,{"derivedFrom":subQ1}),1.0]])]})])]}),"instanceName":"14"});}
            var Q12;
            {var subQ1=sQuery(id+"F2.wireOp",EDGE,"E13.1.0");Q12=makeQuery(id+"F6.opPattern","COPY",BODY,{"derivedFrom":makeQuery(id+"F3.opLoft","SWEPT_BODY",BODY,{"disambiguationData":[OSD([makeQuery(id+"F0.imprint","IMPRINT",FACE,{"disambiguationData":[TD([[makeQuery(id+"F0.imprint","IMPRINT",EDGE,{"derivedFrom":sQuery(id+"F0.wireOp",EDGE,"E1.trimOffspring")}),1.0]])]}),makeQuery(id+"F2.imprint","IMPRINT",FACE,{"disambiguationData":[TD([[makeQuery(id+"F2.imprint","IMPRINT",EDGE,{"derivedFrom":subQ1}),1.0]])]})])]}),"instanceName":"15"});}
            var Q13;
            {var subQ1=sQuery(id+"F2.wireOp",EDGE,"E13.1.0");Q13=makeQuery(id+"F6.opPattern","COPY",BODY,{"derivedFrom":makeQuery(id+"F3.opLoft","SWEPT_BODY",BODY,{"disambiguationData":[OSD([makeQuery(id+"F0.imprint","IMPRINT",FACE,{"disambiguationData":[TD([[makeQuery(id+"F0.imprint","IMPRINT",EDGE,{"derivedFrom":sQuery(id+"F0.wireOp",EDGE,"E1.trimOffspring")}),1.0]])]}),makeQuery(id+"F2.imprint","IMPRINT",FACE,{"disambiguationData":[TD([[makeQuery(id+"F2.imprint","IMPRINT",EDGE,{"derivedFrom":subQ1}),1.0]])]})])]}),"instanceName":"13"});}
            var Q14;
            {var subQ1=sQuery(id+"F2.wireOp",EDGE,"E13.1.0");Q14=makeQuery(id+"F6.opPattern","COPY",BODY,{"derivedFrom":makeQuery(id+"F3.opLoft","SWEPT_BODY",BODY,{"disambiguationData":[OSD([makeQuery(id+"F0.imprint","IMPRINT",FACE,{"disambiguationData":[TD([[makeQuery(id+"F0.imprint","IMPRINT",EDGE,{"derivedFrom":sQuery(id+"F0.wireOp",EDGE,"E1.trimOffspring")}),1.0]])]}),makeQuery(id+"F2.imprint","IMPRINT",FACE,{"disambiguationData":[TD([[makeQuery(id+"F2.imprint","IMPRINT",EDGE,{"derivedFrom":subQ1}),1.0]])]})])]}),"instanceName":"12"});}
            var Q15;
            {var subQ1=sQuery(id+"F2.wireOp",EDGE,"E13.1.0");Q15=makeQuery(id+"F6.opPattern","COPY",BODY,{"derivedFrom":makeQuery(id+"F3.opLoft","SWEPT_BODY",BODY,{"disambiguationData":[OSD([makeQuery(id+"F0.imprint","IMPRINT",FACE,{"disambiguationData":[TD([[makeQuery(id+"F0.imprint","IMPRINT",EDGE,{"derivedFrom":sQuery(id+"F0.wireOp",EDGE,"E1.trimOffspring")}),1.0]])]}),makeQuery(id+"F2.imprint","IMPRINT",FACE,{"disambiguationData":[TD([[makeQuery(id+"F2.imprint","IMPRINT",EDGE,{"derivedFrom":subQ1}),1.0]])]})])]}),"instanceName":"11"});}
            var Q16;
            {var subQ1=sQuery(id+"F2.wireOp",EDGE,"E13.1.0");Q16=makeQuery(id+"F6.opPattern","COPY",BODY,{"derivedFrom":makeQuery(id+"F3.opLoft","SWEPT_BODY",BODY,{"disambiguationData":[OSD([makeQuery(id+"F0.imprint","IMPRINT",FACE,{"disambiguationData":[TD([[makeQuery(id+"F0.imprint","IMPRINT",EDGE,{"derivedFrom":sQuery(id+"F0.wireOp",EDGE,"E1.trimOffspring")}),1.0]])]}),makeQuery(id+"F2.imprint","IMPRINT",FACE,{"disambiguationData":[TD([[makeQuery(id+"F2.imprint","IMPRINT",EDGE,{"derivedFrom":subQ1}),1.0]])]})])]}),"instanceName":"10"});}
            var Q17;
            {var subQ1=sQuery(id+"F2.wireOp",EDGE,"E13.1.0");Q17=makeQuery(id+"F6.opPattern","COPY",BODY,{"derivedFrom":makeQuery(id+"F3.opLoft","SWEPT_BODY",BODY,{"disambiguationData":[OSD([makeQuery(id+"F0.imprint","IMPRINT",FACE,{"disambiguationData":[TD([[makeQuery(id+"F0.imprint","IMPRINT",EDGE,{"derivedFrom":sQuery(id+"F0.wireOp",EDGE,"E1.trimOffspring")}),1.0]])]}),makeQuery(id+"F2.imprint","IMPRINT",FACE,{"disambiguationData":[TD([[makeQuery(id+"F2.imprint","IMPRINT",EDGE,{"derivedFrom":subQ1}),1.0]])]})])]}),"instanceName":"9"});}
            var Q18;
            {var subQ1=sQuery(id+"F2.wireOp",EDGE,"E13.1.0");Q18=makeQuery(id+"F6.opPattern","COPY",BODY,{"derivedFrom":makeQuery(id+"F3.opLoft","SWEPT_BODY",BODY,{"disambiguationData":[OSD([makeQuery(id+"F0.imprint","IMPRINT",FACE,{"disambiguationData":[TD([[makeQuery(id+"F0.imprint","IMPRINT",EDGE,{"derivedFrom":sQuery(id+"F0.wireOp",EDGE,"E1.trimOffspring")}),1.0]])]}),makeQuery(id+"F2.imprint","IMPRINT",FACE,{"disambiguationData":[TD([[makeQuery(id+"F2.imprint","IMPRINT",EDGE,{"derivedFrom":subQ1}),1.0]])]})])]}),"instanceName":"8"});}
            var Q19;
            {var subQ1=sQuery(id+"F2.wireOp",EDGE,"E13.1.0");Q19=makeQuery(id+"F6.opPattern","COPY",BODY,{"derivedFrom":makeQuery(id+"F3.opLoft","SWEPT_BODY",BODY,{"disambiguationData":[OSD([makeQuery(id+"F0.imprint","IMPRINT",FACE,{"disambiguationData":[TD([[makeQuery(id+"F0.imprint","IMPRINT",EDGE,{"derivedFrom":sQuery(id+"F0.wireOp",EDGE,"E1.trimOffspring")}),1.0]])]}),makeQuery(id+"F2.imprint","IMPRINT",FACE,{"disambiguationData":[TD([[makeQuery(id+"F2.imprint","IMPRINT",EDGE,{"derivedFrom":subQ1}),1.0]])]})])]}),"instanceName":"7"});}
            var Q20;
            {var subQ1=sQuery(id+"F2.wireOp",EDGE,"E13.1.0");Q20=makeQuery(id+"F6.opPattern","COPY",BODY,{"derivedFrom":makeQuery(id+"F3.opLoft","SWEPT_BODY",BODY,{"disambiguationData":[OSD([makeQuery(id+"F0.imprint","IMPRINT",FACE,{"disambiguationData":[TD([[makeQuery(id+"F0.imprint","IMPRINT",EDGE,{"derivedFrom":sQuery(id+"F0.wireOp",EDGE,"E1.trimOffspring")}),1.0]])]}),makeQuery(id+"F2.imprint","IMPRINT",FACE,{"disambiguationData":[TD([[makeQuery(id+"F2.imprint","IMPRINT",EDGE,{"derivedFrom":subQ1}),1.0]])]})])]}),"instanceName":"6"});}
            var Q21;
            {var subQ1=sQuery(id+"F2.wireOp",EDGE,"E13.1.0");Q21=makeQuery(id+"F6.opPattern","COPY",BODY,{"derivedFrom":makeQuery(id+"F3.opLoft","SWEPT_BODY",BODY,{"disambiguationData":[OSD([makeQuery(id+"F0.imprint","IMPRINT",FACE,{"disambiguationData":[TD([[makeQuery(id+"F0.imprint","IMPRINT",EDGE,{"derivedFrom":sQuery(id+"F0.wireOp",EDGE,"E1.trimOffspring")}),1.0]])]}),makeQuery(id+"F2.imprint","IMPRINT",FACE,{"disambiguationData":[TD([[makeQuery(id+"F2.imprint","IMPRINT",EDGE,{"derivedFrom":subQ1}),1.0]])]})])]}),"instanceName":"5"});}
            var Q22;
            {var subQ1=sQuery(id+"F2.wireOp",EDGE,"E13.1.0");Q22=makeQuery(id+"F6.opPattern","COPY",BODY,{"derivedFrom":makeQuery(id+"F3.opLoft","SWEPT_BODY",BODY,{"disambiguationData":[OSD([makeQuery(id+"F0.imprint","IMPRINT",FACE,{"disambiguationData":[TD([[makeQuery(id+"F0.imprint","IMPRINT",EDGE,{"derivedFrom":sQuery(id+"F0.wireOp",EDGE,"E1.trimOffspring")}),1.0]])]}),makeQuery(id+"F2.imprint","IMPRINT",FACE,{"disambiguationData":[TD([[makeQuery(id+"F2.imprint","IMPRINT",EDGE,{"derivedFrom":subQ1}),1.0]])]})])]}),"instanceName":"4"});}
            var Q23;
            {var subQ1=sQuery(id+"F2.wireOp",EDGE,"E13.1.0");Q23=makeQuery(id+"F6.opPattern","COPY",BODY,{"derivedFrom":makeQuery(id+"F3.opLoft","SWEPT_BODY",BODY,{"disambiguationData":[OSD([makeQuery(id+"F0.imprint","IMPRINT",FACE,{"disambiguationData":[TD([[makeQuery(id+"F0.imprint","IMPRINT",EDGE,{"derivedFrom":sQuery(id+"F0.wireOp",EDGE,"E1.trimOffspring")}),1.0]])]}),makeQuery(id+"F2.imprint","IMPRINT",FACE,{"disambiguationData":[TD([[makeQuery(id+"F2.imprint","IMPRINT",EDGE,{"derivedFrom":subQ1}),1.0]])]})])]}),"instanceName":"3"});}
            var Q24;
            {var subQ1=sQuery(id+"F2.wireOp",EDGE,"E13.1.0");Q24=makeQuery(id+"F6.opPattern","COPY",BODY,{"derivedFrom":makeQuery(id+"F3.opLoft","SWEPT_BODY",BODY,{"disambiguationData":[OSD([makeQuery(id+"F0.imprint","IMPRINT",FACE,{"disambiguationData":[TD([[makeQuery(id+"F0.imprint","IMPRINT",EDGE,{"derivedFrom":sQuery(id+"F0.wireOp",EDGE,"E1.trimOffspring")}),1.0]])]}),makeQuery(id+"F2.imprint","IMPRINT",FACE,{"disambiguationData":[TD([[makeQuery(id+"F2.imprint","IMPRINT",EDGE,{"derivedFrom":subQ1}),1.0]])]})])]}),"instanceName":"2"});}
            booleanBodies(context, id + "F7", {"operationType" : BooleanOperationType.UNION, "tools" : qUnion([Q0, Q1, Q2, Q3, Q4, Q5, Q6, Q7, Q8, Q9, Q10, Q11, Q12, Q13, Q14, Q15, Q16, Q17, Q18, Q19, Q20, Q21, Q22, Q23, Q24])});
        }
        {
            var Q0;
            {var subQ1=sQuery(id+"F2.wireOp",EDGE,"E13.1.0");var subQ3=makeQuery(id+"F5.boolean.opBoolean","MERGE",FACE,{"derivedFrom":[makeQuery(id+"F3.opLoft","CAP_FACE",FACE,{"disambiguationData":[OSD([makeQuery(id+"F2.imprint","IMPRINT",FACE,{"disambiguationData":[TD([[makeQuery(id+"F2.imprint","IMPRINT",EDGE,{"derivedFrom":subQ1}),1.0]])]})])],"isStart":true}),makeQuery(id+"F5.opExtrude","CAP_FACE",FACE,{"disambiguationData":[OSD([sQuery(id+"F4.wireOp",EDGE,"E14")])],"isStart":true})]});Q0=makeQuery(id+"F7.opBoolean","MERGE",FACE,{"derivedFrom":[subQ3,makeQuery(id+"F6.opPattern","COPY",FACE,{"derivedFrom":subQ3,"instanceName":"1"}),makeQuery(id+"F6.opPattern","COPY",FACE,{"derivedFrom":subQ3,"instanceName":"2"}),makeQuery(id+"F6.opPattern","COPY",FACE,{"derivedFrom":subQ3,"instanceName":"3"}),makeQuery(id+"F6.opPattern","COPY",FACE,{"derivedFrom":subQ3,"instanceName":"4"}),makeQuery(id+"F6.opPattern","COPY",FACE,{"derivedFrom":subQ3,"instanceName":"5"}),makeQuery(id+"F6.opPattern","COPY",FACE,{"derivedFrom":subQ3,"instanceName":"6"}),makeQuery(id+"F6.opPattern","COPY",FACE,{"derivedFrom":subQ3,"instanceName":"7"}),makeQuery(id+"F6.opPattern","COPY",FACE,{"derivedFrom":subQ3,"instanceName":"8"}),makeQuery(id+"F6.opPattern","COPY",FACE,{"derivedFrom":subQ3,"instanceName":"9"}),makeQuery(id+"F6.opPattern","COPY",FACE,{"derivedFrom":subQ3,"instanceName":"10"}),makeQuery(id+"F6.opPattern","COPY",FACE,{"derivedFrom":subQ3,"instanceName":"11"}),makeQuery(id+"F6.opPattern","COPY",FACE,{"derivedFrom":subQ3,"instanceName":"12"}),makeQuery(id+"F6.opPattern","COPY",FACE,{"derivedFrom":subQ3,"instanceName":"13"}),makeQuery(id+"F6.opPattern","COPY",FACE,{"derivedFrom":subQ3,"instanceName":"14"}),makeQuery(id+"F6.opPattern","COPY",FACE,{"derivedFrom":subQ3,"instanceName":"15"}),makeQuery(id+"F6.opPattern","COPY",FACE,{"derivedFrom":subQ3,"instanceName":"16"}),makeQuery(id+"F6.opPattern","COPY",FACE,{"derivedFrom":subQ3,"instanceName":"17"}),makeQuery(id+"F6.opPattern","COPY",FACE,{"derivedFrom":subQ3,"instanceName":"18"}),makeQuery(id+"F6.opPattern","COPY",FACE,{"derivedFrom":subQ3,"instanceName":"19"}),makeQuery(id+"F6.opPattern","COPY",FACE,{"derivedFrom":subQ3,"instanceName":"20"}),makeQuery(id+"F6.opPattern","COPY",FACE,{"derivedFrom":subQ3,"instanceName":"21"}),makeQuery(id+"F6.opPattern","COPY",FACE,{"derivedFrom":subQ3,"instanceName":"22"}),makeQuery(id+"F6.opPattern","COPY",FACE,{"derivedFrom":subQ3,"instanceName":"23"})]});}
            var sketch = newSketch(context, id + "F8", { "sketchPlane" : qUnion([Q0])});
            skPoint(sketch, "E15", {"position": v(0, 0) * mm});
            skSolve(sketch);
        }
        {
            var Q0;
            Q0=sQuery(id+"F8.wireOp",VERTEX,"E15");
            var Q1;
            {var subQ1=sQuery(id+"F2.wireOp",EDGE,"E13.1.0");Q1=makeQuery(id+"F3.opLoft","SWEPT_BODY",BODY,{"disambiguationData":[OSD([makeQuery(id+"F0.imprint","IMPRINT",FACE,{"disambiguationData":[TD([[makeQuery(id+"F0.imprint","IMPRINT",EDGE,{"derivedFrom":sQuery(id+"F0.wireOp",EDGE,"E1.trimOffspring")}),1.0]])]}),makeQuery(id+"F2.imprint","IMPRINT",FACE,{"disambiguationData":[TD([[makeQuery(id+"F2.imprint","IMPRINT",EDGE,{"derivedFrom":subQ1}),1.0]])]})])]});}
            hole(context, id + "F9", {"style" : HoleStyle.SIMPLE, "endStyle" : HoleEndStyle.THROUGH, "holeDiameter" : 12.7 * mm, "tappedDepth" : 12.7 * mm, "tapClearance" : 3, "locations" : qUnion([Q0]), "scope" : qUnion([Q1])});
        }
    });
